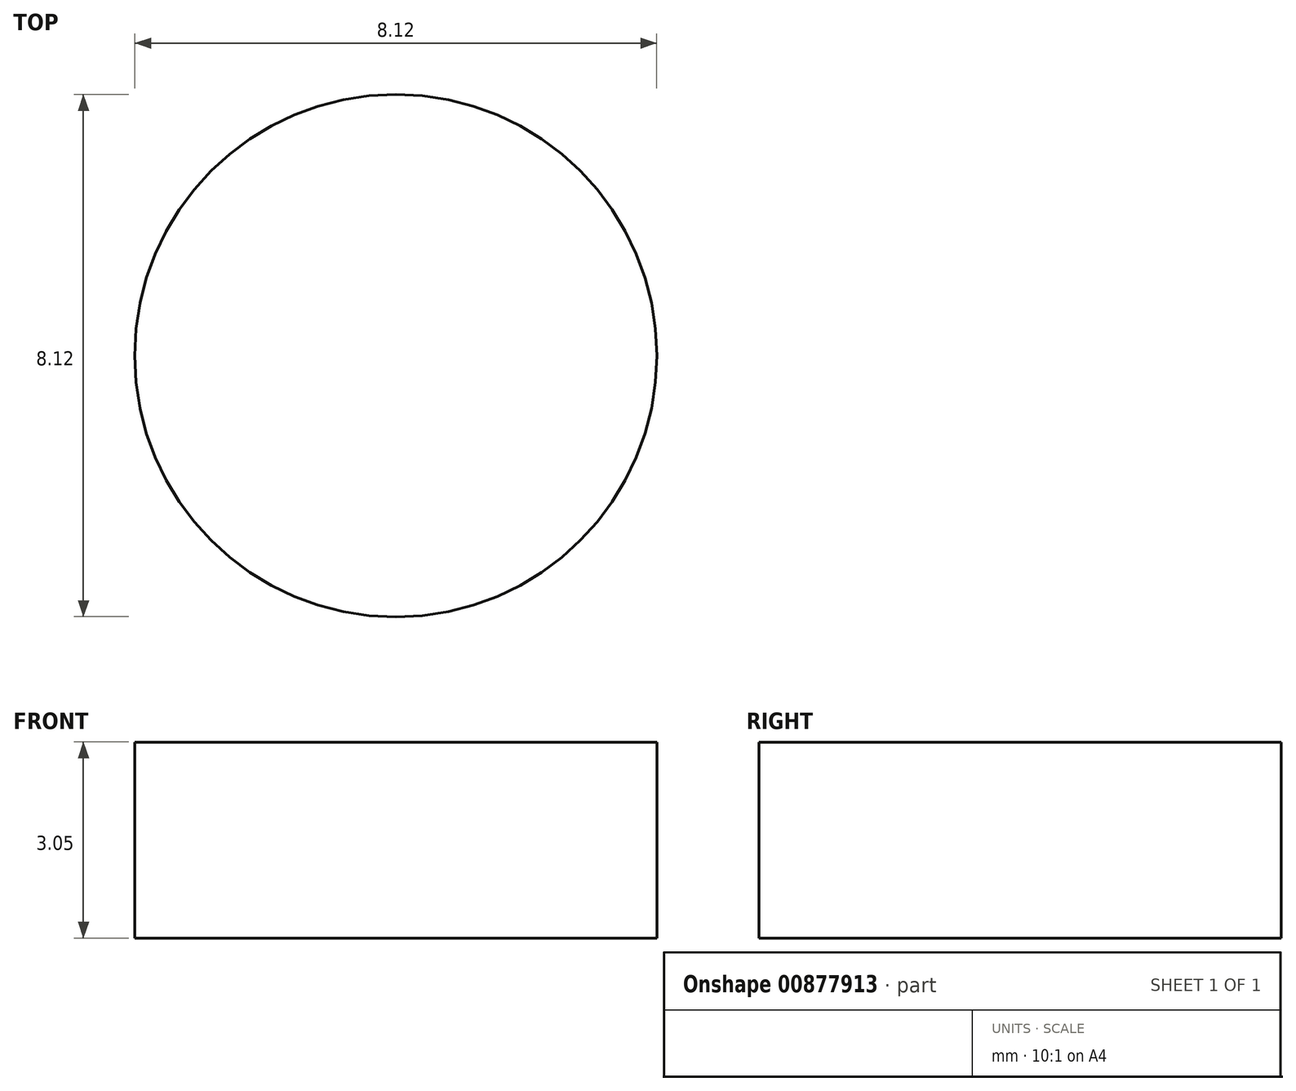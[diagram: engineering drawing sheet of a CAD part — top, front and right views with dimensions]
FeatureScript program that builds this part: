
annotation { "Feature Type Name" : "Feature", "Feature Type Description" : "" }
export const myFeature = defineFeature(function(context is Context, id is Id, definition is map)
    precondition{}
    {
        {
            var Q0;
            Q0=qCreatedBy(makeId("Top.planeOp"),FACE);
            var sketch = newSketch(context, id + "F0", { "sketchPlane" : qUnion([Q0])});
            skCircle(sketch, "E0", {"center": v(0, 0) * mm, "radius": 4.06 * mm});
            skSolve(sketch);
        }
        {
            var Q0;
            Q0 = qSketchRegion(id + "F0", true);
            extrude(context, id + "F1", {"entities" : qUnion([Q0]), "depth" : 3.05 * mm, "offsetDistance" : 25.4 * mm});
        }
    });
